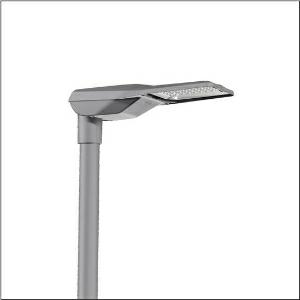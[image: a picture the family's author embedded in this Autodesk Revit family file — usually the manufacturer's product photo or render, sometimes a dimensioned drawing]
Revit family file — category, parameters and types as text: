
# Revit family: streetlight_sl_21_iq_mini___p0_8a_5xe2u31g08hb_4850
name_source: partatom
category: Lighting Fixtures
units: mm (PartAtom-declared; Revit-internal decimal feet)

## family parameters
Cut with Voids When Loaded = No
Host = Face
Light Source = No
Part Type = Normal
Room Calculation Point = No
Round Connector Dimension = Use Diameter
Shared = No

## types (1)
- --- (1 x LED, 9540 lm, 70.9 W, 3000K)
    Apparent Load = 71 VA
    CIE Flux Codes = 33 69 96 100 100
    Color Rendering = 70
    Color Temperature = 3000K
    Default Elevation = 1800 mm
    Description = Streetlight SL 21 iQ mini, mast luminaire, primary light control with lens, of PMMA, primary optical cover: cover, of toughened safety glass, transparent, light distribution: P0.8a, light emission: direct distribution, primary light characteristic: asymmetric, installation type: post-top, side-entry, LED, High Power LED, rated luminous flux: 9.540lm, luminous efficacy: 135lm/W, light colour: 730, colour temperature: 3000K, control gear: iQ Street-Remote, control: pre-setting: linear dimming characteristic, Street-Remote, Auto-Match, Temp-Guard, Lumen-Switch, Night-Set, Smart-Wire, Light-Fading, Desk-Remote (wireless, voltage-free reading and setting of iQ features in the workshop via application-optimized NFC function/RFID function), optimised constant luminous flux control (CLO 2.0), mains connection: 220..240V, AC, 50/60Hz, start of lifetime: 71W, end of service life: 75W, reduction: 31W, luminaire housing, of diecast aluminium, powder-coated, Siteco® metallic grey (DB 702S), corrosivity category C5 mid according to DIN EN ISO 12944, please order mast flange separately, inclination adjustable: 0°, 5°, 10°, 15°, sealing non-destructively replaceable, multi-level sealing system, length: 628mm, width: 235mm, height: 110mm, mast flange for spigot size: 42mm (side-entry): 5XC10008XM4, 60/48mm (side-entry/post-top): 5XC10108XM2, 76/60mm (side-entry/post-top): 5XC10108XM1, mounting height: 4..8m, protection rating (complete): IP66, insulation class (complete): insulation class II (safety insulation), certification: CE, ENEC, ENEC+, VDE, impact resistance: IK10, permissible operating ambient temperature for outdoor applications: -40..+50°C, standard-compliant lighting for roads and squares, packaging unit: 1 piece

Light Distribution: P0.8a
    Height = 110 mm
    Lamp = 1 x LED
    Lamp Light Flux = 9540 lm
    Lamp Power = 70.9 W
    Lamp count = 1
    Length = 625 mm
    Luminous efficacy = 135 lm/W
    Manufacturer = Siteco
    ModVariant = No
    Model = 5XE2U31G08HB
    Number of Poles = 1
    OnlyDefault = Yes
    Power Factor = 1
    Product Name = Streetlight SL 21 iQ mini | P0.8a
    Product group = mast luminaire | pylon top
    ProductGroupID = 6100
    Protection Class = Protection class II
    Protection Degree = IP 66
    RLX_Detail_Level = 1
    RLX_Emergency_Light_Flux = 0 lm
    RLX_Emergency_Type = 0
    RLX_Emergency_Type_DB = No
    RlxData = <blob elided: 26093 chars, md5=4108408b>
    Socket = socket
    Standby Power = 0 W
    System Light Flux = 9540 lm
    System Power = 71 W
    Type Comments = factory setting: luminous flux: 100 % | dim-lin: 254 | 711 mA
    Type Image = l_1003519.jpg
    URL = http://relux.com
    VarID = @adj_072402
    Voltage = 0 V
    Weight = 0.00 kg
    Width = 234 mm

## geometry (parser evidence)
native form markers: Blend x4, Sweep x12
no freeform markers — native parametric forms only
